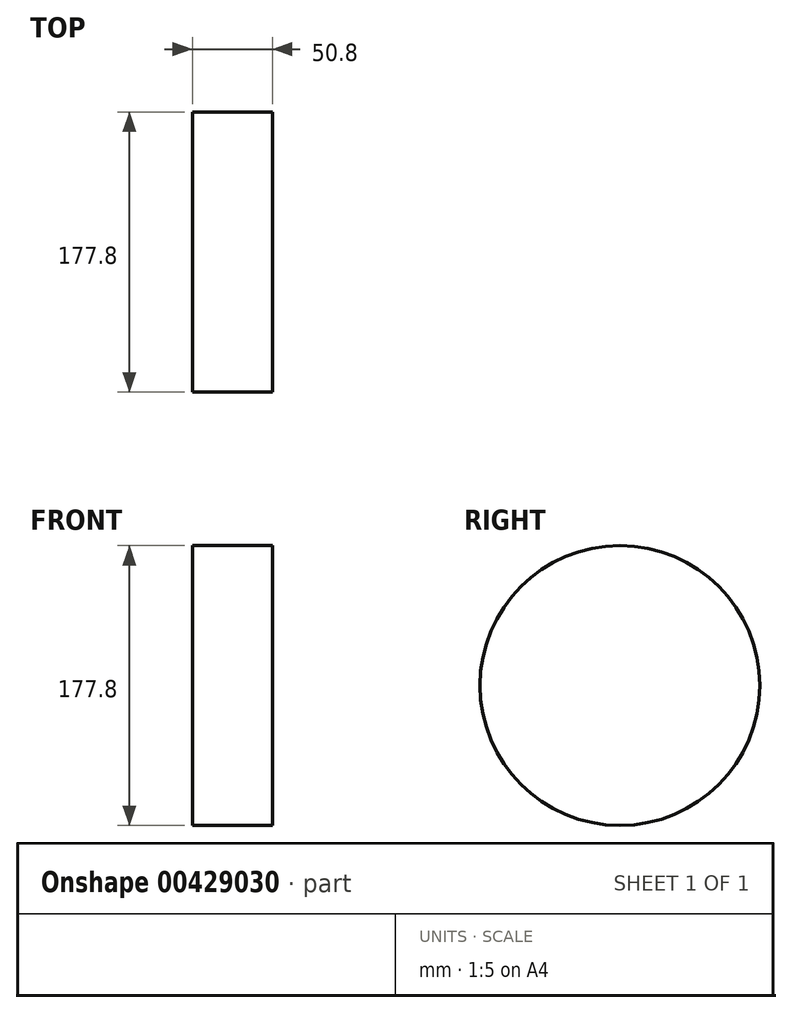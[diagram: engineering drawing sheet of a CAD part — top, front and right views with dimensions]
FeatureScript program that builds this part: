
annotation { "Feature Type Name" : "Feature", "Feature Type Description" : "" }
export const myFeature = defineFeature(function(context is Context, id is Id, definition is map)
    precondition{}
    {
        {
            var Q0;
            Q0=qCreatedBy(makeId("Right.planeOp"),FACE);
            var sketch = newSketch(context, id + "F0", { "sketchPlane" : qUnion([Q0])});
            skCircle(sketch, "E0", {"center": v(0, 0) * mm, "radius": 88.9 * mm});
            skSolve(sketch);
        }
        {
            var Q0;
            Q0=makeQuery(id+"F0.imprint","IMPRINT",FACE,{"disambiguationData":[TD([[makeQuery(id+"F0.imprint","IMPRINT",EDGE,{"derivedFrom":sQuery(id+"F0.wireOp",EDGE,"E0")}),1.0]])]});
            extrude(context, id + "F1", {"entities" : qUnion([Q0]), "depth" : 25.4 * mm});
        }
        {
            var Q0;
            Q0=makeQuery(id+"F1.opExtrude","SWEPT_BODY",BODY,{"disambiguationData":[OSD([sQuery(id+"F0.wireOp",EDGE,"E0")])]});
            var Q1;
            Q1=makeQuery(id+"F1.opExtrude","CAP_FACE",FACE,{"disambiguationData":[OSD([sQuery(id+"F0.wireOp",EDGE,"E0")])],"isStart":false});
            mirror(context, id + "F2", {"operationType" : NewBodyOperationType.ADD, "entities" : qUnion([Q0]), "mirrorPlane" : qUnion([Q1])});
        }
    });
